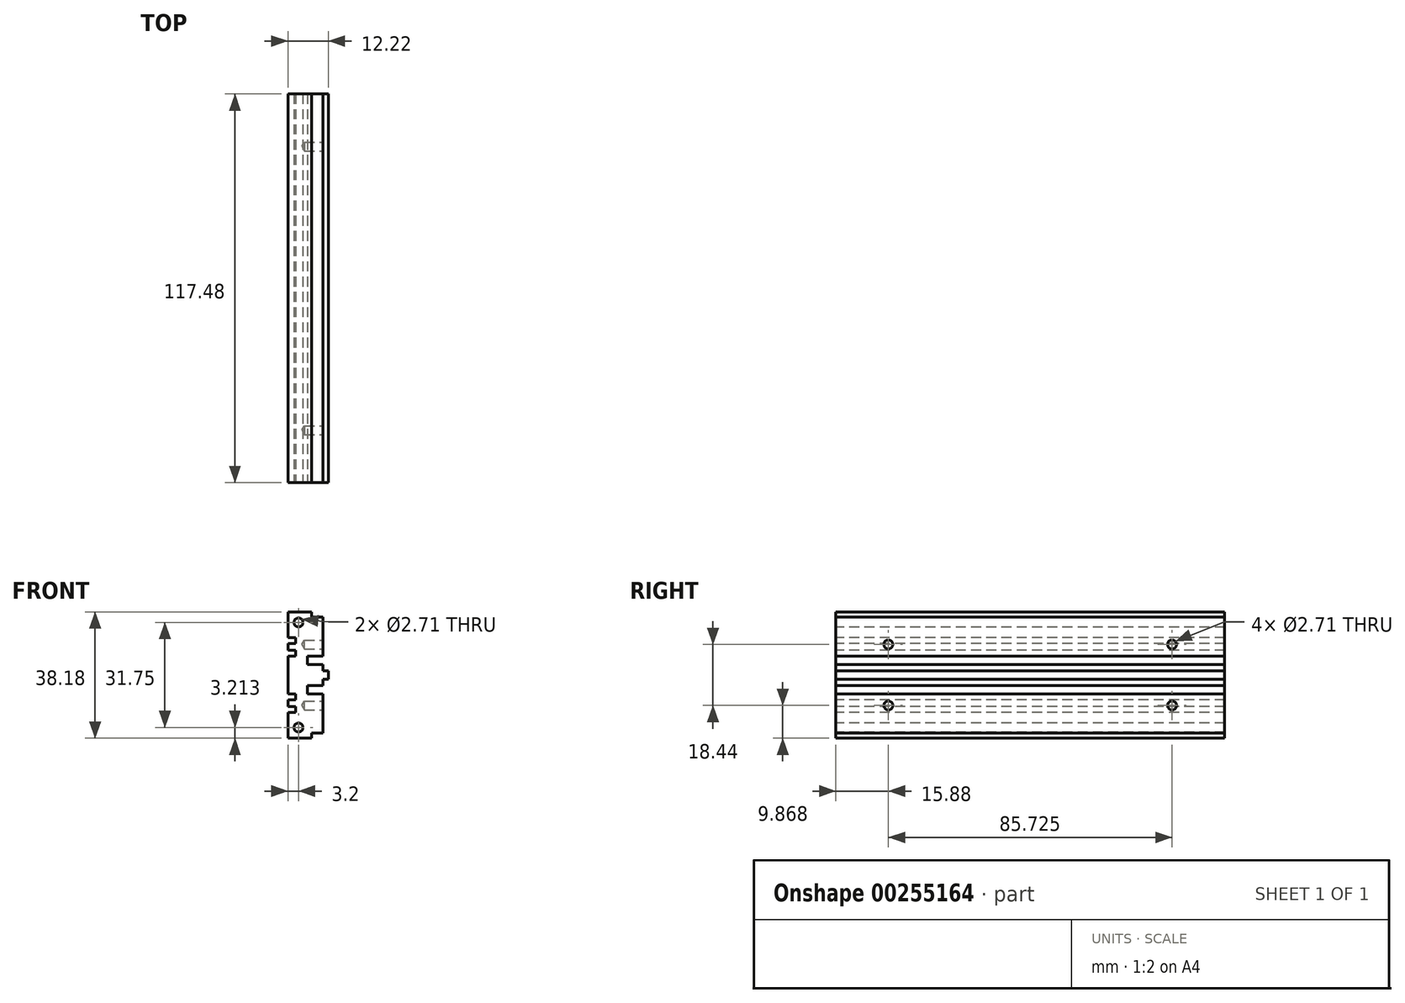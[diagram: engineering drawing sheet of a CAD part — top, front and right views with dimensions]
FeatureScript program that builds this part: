
annotation { "Feature Type Name" : "Feature", "Feature Type Description" : "" }
export const myFeature = defineFeature(function(context is Context, id is Id, definition is map)
    precondition{}
    {
        {
            var Q0;
            Q0=qCreatedBy(makeId("Front.planeOp"),FACE);
            var sketch = newSketch(context, id + "F0", { "sketchPlane" : qUnion([Q0])});
            skLineSegment(sketch, "E0.bottom", {"start": v(0, 0) * mm, "end": v(12.22, 0) * mm});
            skLineSegment(sketch, "E0.top", {"start": v(0, 38.18) * mm, "end": v(12.22, 38.18) * mm});
            skLineSegment(sketch, "E0.left", {"start": v(0, 0) * mm, "end": v(0, 38.18) * mm});
            skLineSegment(sketch, "E0.right", {"start": v(12.22, 0) * mm, "end": v(12.22, 38.18) * mm});
            skSolve(sketch);
        }
        {
            var Q0;
            Q0 = qSketchRegion(id + "F0", true);
            extrude(context, id + "F1", {"entities" : qUnion([Q0]), "depth" : 117.47 * mm});
        }
        {
            var Q0;
            Q0=makeQuery(id+"F1.opExtrude","CAP_FACE",FACE,{"disambiguationData":[OSD([sQuery(id+"F0.wireOp",EDGE,"E0.bottom"),sQuery(id+"F0.wireOp",EDGE,"E0.top"),sQuery(id+"F0.wireOp",EDGE,"E0.left"),sQuery(id+"F0.wireOp",EDGE,"E0.right")])],"isStart":false});
            var sketch = newSketch(context, id + "F2", { "sketchPlane" : qUnion([Q0])});
            skLineSegment(sketch, "E1", {"start": v(0, 19.09) * mm, "end": v(12.22, 19.09) * mm, "construction": true});
            skLineSegment(sketch, "E2.bottom", {"start": v(0, 30.4) * mm, "end": v(2.29, 30.4) * mm});
            skLineSegment(sketch, "E2.top", {"start": v(0, 28.61) * mm, "end": v(2.29, 28.61) * mm});
            skLineSegment(sketch, "E2.left", {"start": v(0, 30.4) * mm, "end": v(0, 28.61) * mm});
            skLineSegment(sketch, "E2.right", {"start": v(2.29, 30.4) * mm, "end": v(2.29, 28.61) * mm});
            skLineSegment(sketch, "E3.bottom", {"start": v(0, 26.58) * mm, "end": v(2.29, 26.58) * mm});
            skLineSegment(sketch, "E3.top", {"start": v(0, 24.8) * mm, "end": v(2.29, 24.8) * mm});
            skLineSegment(sketch, "E3.left", {"start": v(0, 26.58) * mm, "end": v(0, 24.8) * mm});
            skLineSegment(sketch, "E3.right", {"start": v(2.29, 26.58) * mm, "end": v(2.29, 24.8) * mm});
            skLineSegment(sketch, "E4", {"start": v(0, 29.5) * mm, "end": v(2.29, 29.5) * mm, "construction": true});
            skLineSegment(sketch, "E5", {"start": v(0, 25.7) * mm, "end": v(2.29, 25.7) * mm, "construction": true});
            skLineSegment(sketch, "E6.MirrorCS", {"start": v(2.29, 7.79) * mm, "end": v(2.29, 9.56) * mm});
            skLineSegment(sketch, "E7.MirrorCS", {"start": v(0, 7.79) * mm, "end": v(0, 9.56) * mm});
            skLineSegment(sketch, "E8.MirrorCS", {"start": v(2.29, 11.6) * mm, "end": v(2.29, 13.37) * mm});
            skLineSegment(sketch, "E9.MirrorCS", {"start": v(0, 11.6) * mm, "end": v(0, 13.37) * mm});
            skLineSegment(sketch, "E10.MirrorCS", {"start": v(0, 8.67) * mm, "end": v(2.29, 8.67) * mm, "construction": true});
            skLineSegment(sketch, "E11.MirrorCS", {"start": v(0, 12.48) * mm, "end": v(2.29, 12.48) * mm, "construction": true});
            skLineSegment(sketch, "E12.MirrorCS", {"start": v(0, 13.37) * mm, "end": v(2.29, 13.37) * mm});
            skLineSegment(sketch, "E13.MirrorCS", {"start": v(0, 11.6) * mm, "end": v(2.29, 11.6) * mm});
            skLineSegment(sketch, "E14.MirrorCS", {"start": v(0, 9.56) * mm, "end": v(2.29, 9.56) * mm});
            skLineSegment(sketch, "E15.MirrorCS", {"start": v(0, 7.79) * mm, "end": v(2.29, 7.79) * mm});
            skSolve(sketch);
        }
        {
            var Q0;
            Q0 = qSketchRegion(id + "F2", true);
            extrude(context, id + "F3", {"entities" : qUnion([Q0]), "operationType" : NewBodyOperationType.REMOVE, "endBound" : BoundingType.THROUGH_ALL, "oppositeDirection" : true, "depth" : 25.4 * mm});
        }
        {
            var Q0;
            Q0=makeQuery(id+"F1.opExtrude","CAP_FACE",FACE,{"disambiguationData":[OSD([sQuery(id+"F0.wireOp",EDGE,"E0.bottom"),sQuery(id+"F0.wireOp",EDGE,"E0.top"),sQuery(id+"F0.wireOp",EDGE,"E0.left"),sQuery(id+"F0.wireOp",EDGE,"E0.right")])],"isStart":false});
            var sketch = newSketch(context, id + "F4", { "sketchPlane" : qUnion([Q0])});
            skLineSegment(sketch, "E16", {"start": v(0, 19.09) * mm, "end": v(12.22, 19.09) * mm, "construction": true});
            skLineSegment(sketch, "E17", {"start": v(12.22, 20.36) * mm, "end": v(10.57, 20.36) * mm});
            skLineSegment(sketch, "E18", {"start": v(10.57, 20.36) * mm, "end": v(10.57, 22.26) * mm});
            skLineSegment(sketch, "E19", {"start": v(10.57, 22.26) * mm, "end": v(5.87, 22.26) * mm});
            skLineSegment(sketch, "E20", {"start": v(5.87, 22.26) * mm, "end": v(5.87, 24.8) * mm});
            skLineSegment(sketch, "E21", {"start": v(5.87, 24.8) * mm, "end": v(10.57, 24.8) * mm});
            skLineSegment(sketch, "E22", {"start": v(10.57, 24.8) * mm, "end": v(10.57, 36.65) * mm});
            skLineSegment(sketch, "E23", {"start": v(10.57, 36.65) * mm, "end": v(7.14, 36.65) * mm});
            skLineSegment(sketch, "E24", {"start": v(7.14, 36.65) * mm, "end": v(7.14, 38.18) * mm});
            skLineSegment(sketch, "E25.MirrorCS", {"start": v(10.57, 1.52) * mm, "end": v(7.14, 1.52) * mm});
            skLineSegment(sketch, "E26.MirrorCS", {"start": v(7.14, 1.52) * mm, "end": v(7.14, 0) * mm});
            skLineSegment(sketch, "E27.MirrorCS", {"start": v(10.57, 13.37) * mm, "end": v(10.57, 1.52) * mm});
            skLineSegment(sketch, "E28.MirrorCS", {"start": v(5.87, 13.37) * mm, "end": v(10.57, 13.37) * mm});
            skLineSegment(sketch, "E29.MirrorCS", {"start": v(5.87, 15.91) * mm, "end": v(5.87, 13.37) * mm});
            skLineSegment(sketch, "E30.MirrorCS", {"start": v(10.57, 15.91) * mm, "end": v(5.87, 15.91) * mm});
            skLineSegment(sketch, "E31.MirrorCS", {"start": v(12.22, 17.82) * mm, "end": v(10.57, 17.82) * mm});
            skLineSegment(sketch, "E32.MirrorCS", {"start": v(10.57, 17.82) * mm, "end": v(10.57, 15.91) * mm});
            skLineSegment(sketch, "E33", {"start": v(12.22, 20.36) * mm, "end": v(12.22, 38.18) * mm});
            skLineSegment(sketch, "E34", {"start": v(12.22, 38.18) * mm, "end": v(7.14, 38.18) * mm});
            skLineSegment(sketch, "E35", {"start": v(12.22, 17.82) * mm, "end": v(12.22, 0) * mm});
            skLineSegment(sketch, "E36", {"start": v(12.22, 0) * mm, "end": v(7.14, 0) * mm});
            skSolve(sketch);
        }
        {
            var Q0;
            Q0 = qSketchRegion(id + "F4", true);
            extrude(context, id + "F5", {"entities" : qUnion([Q0]), "operationType" : NewBodyOperationType.REMOVE, "endBound" : BoundingType.THROUGH_ALL, "oppositeDirection" : true, "depth" : 25.4 * mm});
        }
        {
            var Q0;
            Q0=makeQuery(id+"F1.opExtrude","CAP_FACE",FACE,{"disambiguationData":[OSD([sQuery(id+"F0.wireOp",EDGE,"E0.bottom"),sQuery(id+"F0.wireOp",EDGE,"E0.top"),sQuery(id+"F0.wireOp",EDGE,"E0.left"),sQuery(id+"F0.wireOp",EDGE,"E0.right")])],"isStart":false});
            var sketch = newSketch(context, id + "F6", { "sketchPlane" : qUnion([Q0])});
            skCircle(sketch, "E37", {"center": v(3.2, 3.21) * mm, "radius": 1.27 * mm});
            skCircle(sketch, "E38", {"center": v(3.2, 34.96) * mm, "radius": 1.27 * mm});
            skSolve(sketch);
        }
        {
            var Q0;
            Q0=sQuery(id+"F6.wireOp",VERTEX,"E38.center");
            var Q1;
            Q1=sQuery(id+"F6.wireOp",VERTEX,"E37.center");
            var Q2;
            Q2=makeQuery(id+"F1.opExtrude","SWEPT_BODY",BODY,{"disambiguationData":[OSD([sQuery(id+"F0.wireOp",EDGE,"E0.bottom"),sQuery(id+"F0.wireOp",EDGE,"E0.top"),sQuery(id+"F0.wireOp",EDGE,"E0.left"),sQuery(id+"F0.wireOp",EDGE,"E0.right")])]});
            hole(context, id + "F7", {"style" : HoleStyle.SIMPLE, "endStyle" : HoleEndStyle.THROUGH, "standardTappedOrClearance" : lookupTablePath({ "standard" : "ANSI", "engagement" : "75%", "pitch" : "32 tpi", "size" : "#6", "type" : "Tapped" }), "standardBlindInLast" : lookupTablePath({ "standard" : "ANSI", "engagement" : "75%", "pitch" : "32 tpi", "size" : "#6", "type" : "Tapped" }), "holeDiameter" : 2.7 * mm, "showTappedDepth" : true, "tappedDepth" : 12.7 * mm, "tapClearance" : 3, "locations" : qUnion([Q0, Q1]), "scope" : qUnion([Q2]), "majorDiameter" : 3.5 * mm});
        }
        {
            var Q0;
            Q0=makeQuery(id+"F5.boolean.opBoolean","COPY",FACE,{"derivedFrom":makeQuery(id+"F5.opExtrude","SWEPT_FACE",FACE,{"disambiguationData":[OSD([sQuery(id+"F4.wireOp",EDGE,"E22")])]})});
            var sketch = newSketch(context, id + "F8", { "sketchPlane" : qUnion([Q0])});
            skPoint(sketch, "E39", {"position": v(-101.6, 28.3) * mm});
            skPoint(sketch, "E40", {"position": v(-15.88, 28.3) * mm});
            skLineSegment(sketch, "E41", {"start": v(-58.74, 36.65) * mm, "end": v(-58.74, 24.8) * mm, "construction": true});
            skSolve(sketch);
        }
        {
            var Q0;
            Q0=makeQuery(id+"F5.boolean.opBoolean","COPY",FACE,{"derivedFrom":makeQuery(id+"F5.opExtrude","SWEPT_FACE",FACE,{"disambiguationData":[OSD([sQuery(id+"F4.wireOp",EDGE,"E27.MirrorCS")])]})});
            var sketch = newSketch(context, id + "F9", { "sketchPlane" : qUnion([Q0])});
            skPoint(sketch, "E42", {"position": v(-101.6, 9.87) * mm});
            skPoint(sketch, "E43", {"position": v(-15.88, 9.87) * mm});
            skSolve(sketch);
        }
        {
            var Q0;
            Q0=sQuery(id+"F8.wireOp",VERTEX,"E39");
            var Q1;
            Q1=sQuery(id+"F8.wireOp",VERTEX,"E40");
            var Q2;
            Q2=sQuery(id+"F9.wireOp",VERTEX,"E43");
            var Q3;
            Q3=sQuery(id+"F9.wireOp",VERTEX,"E42");
            var Q4;
            Q4=makeQuery(id+"F1.opExtrude","SWEPT_BODY",BODY,{"disambiguationData":[OSD([sQuery(id+"F0.wireOp",EDGE,"E0.bottom"),sQuery(id+"F0.wireOp",EDGE,"E0.top"),sQuery(id+"F0.wireOp",EDGE,"E0.left"),sQuery(id+"F0.wireOp",EDGE,"E0.right")])]});
            hole(context, id + "F10", {"style" : HoleStyle.SIMPLE, "endStyle" : HoleEndStyle.BLIND, "standardTappedOrClearance" : lookupTablePath({ "standard" : "ANSI", "engagement" : "75%", "pitch" : "32 tpi", "size" : "#6", "type" : "Tapped" }), "standardBlindInLast" : lookupTablePath({ "standard" : "ANSI", "engagement" : "75%", "pitch" : "32 tpi", "size" : "#6", "type" : "Tapped" }), "holeDiameter" : 2.7 * mm, "showTappedDepth" : true, "holeDepth" : 5.56 * mm, "tappedDepth" : 3.17 * mm, "tapClearance" : 3, "locations" : qUnion([Q0, Q1, Q2, Q3]), "scope" : qUnion([Q4]), "majorDiameter" : 3.5 * mm});
        }
    });
